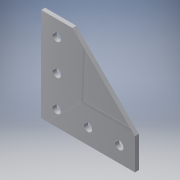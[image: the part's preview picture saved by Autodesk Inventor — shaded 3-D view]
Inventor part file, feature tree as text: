
AUTODESK INVENTOR PART (.ipt)
format: ipt  version: 2016 (Build 200138000, 138)  size: 111,616 bytes
history: native  units: in
note: dims shown in document units (in); Inventor stores cm internally (conversion verified against a paired STEP export)
features: extrude x1, sketch x1
ambient origin geometry x8: Origin, YZ Plane, XZ Plane, XY Plane, X Axis, Y Axis, Z Axis, Center Point
bodies: Solid1 (feature_tree)
feature tree (2):
  extrude  "Extrusion1"  Depth=0.125in
  sketch  "Sketch1"  dims[d0=3.0in d1=1.0in d2=1.0in d3=3.0in d6=0.2656in d10=1.5in d11=2.5in d12=1.5in d15=0.5in d16=0.5in d17=2.5in d18=0.125in d19=0.0in]
